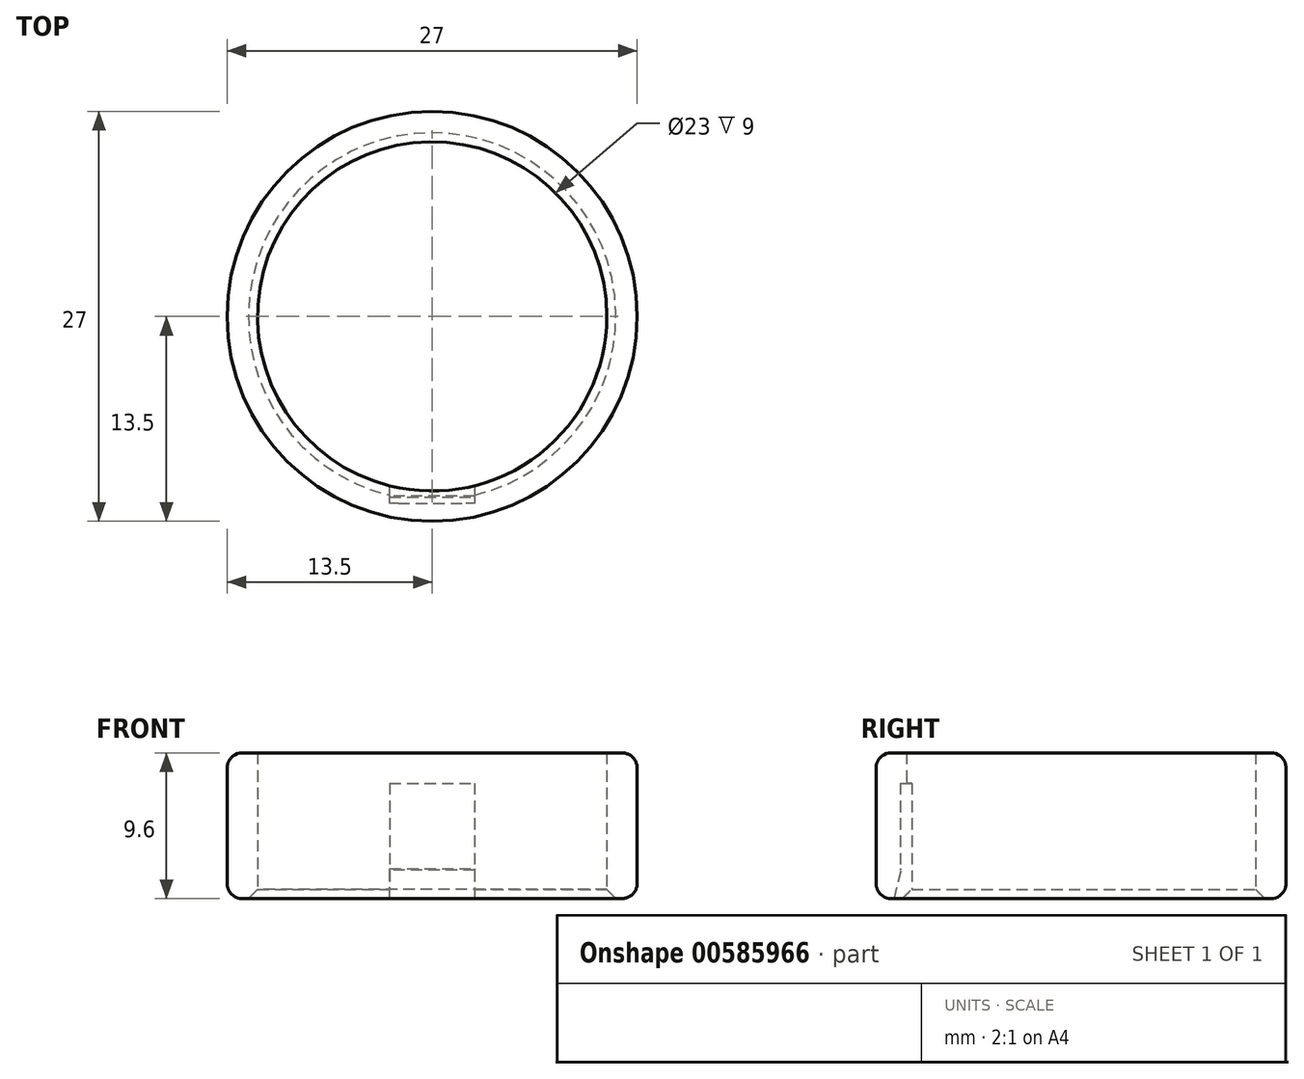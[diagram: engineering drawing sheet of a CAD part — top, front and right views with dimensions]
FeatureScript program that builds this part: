
annotation { "Feature Type Name" : "Feature", "Feature Type Description" : "" }
export const myFeature = defineFeature(function(context is Context, id is Id, definition is map)
    precondition{}
    {
        {
            var Q0;
            Q0=qCreatedBy(makeId("Top.planeOp"),FACE);
            var sketch = newSketch(context, id + "F0", { "sketchPlane" : qUnion([Q0])});
            skCircle(sketch, "E0", {"center": v(0, 0) * mm, "radius": 11.5 * mm});
            skCircle(sketch, "E1", {"center": v(0, 0) * mm, "radius": 13.5 * mm});
            skSolve(sketch);
        }
        {
            var Q0;
            Q0=makeQuery(id+"F0.imprint","IMPRINT",FACE,{"disambiguationData":[TD([[makeQuery(id+"F0.imprint","IMPRINT",EDGE,{"derivedFrom":sQuery(id+"F0.wireOp",EDGE,"E0")}),-1.0]])]});
            extrude(context, id + "F1", {"entities" : qUnion([Q0]), "depth" : 9.6 * mm, "offsetDistance" : 25 * mm});
        }
        {
            var Q0;
            Q0=makeQuery(id+"F0.imprint","IMPRINT",FACE,{"disambiguationData":[TD([[makeQuery(id+"F0.imprint","IMPRINT",EDGE,{"derivedFrom":sQuery(id+"F0.wireOp",EDGE,"E0")}),1.0]])]});
            var sketch = newSketch(context, id + "F2", { "sketchPlane" : qUnion([Q0])});
            skLineSegment(sketch, "E2", {"start": v(0, 0) * mm, "end": v(0, -11.5) * mm, "construction": true});
            skLineSegment(sketch, "E3", {"start": v(0, -11.5) * mm, "end": v(2.8, -11.5) * mm, "construction": true});
            skLineSegment(sketch, "E4", {"start": v(2.8, -11.5) * mm, "end": v(2.8, -12.3) * mm});
            skLineSegment(sketch, "E5", {"start": v(2.8, -12.3) * mm, "end": v(-2.8, -12.3) * mm});
            skLineSegment(sketch, "E6", {"start": v(-2.8, -12.3) * mm, "end": v(-2.8, -11.5) * mm});
            skLineSegment(sketch, "E7", {"start": v(-2.8, -11.5) * mm, "end": v(0, -11.5) * mm, "construction": true});
            skLineSegment(sketch, "E8", {"start": v(-2.8, -11.5) * mm, "end": v(-2.8, -11.1) * mm});
            skLineSegment(sketch, "E9", {"start": v(-2.8, -11.1) * mm, "end": v(2.8, -11.1) * mm});
            skLineSegment(sketch, "E10", {"start": v(2.8, -11.1) * mm, "end": v(2.8, -11.5) * mm});
            skSolve(sketch);
        }
        {
            var Q0;
            Q0 = qSketchRegion(id + "F2", true);
            extrude(context, id + "F3", {"entities" : qUnion([Q0]), "operationType" : NewBodyOperationType.REMOVE, "depth" : 7.6 * mm, "offsetDistance" : 25 * mm});
        }
        {
            var Q0;
            Q0=makeQuery(id+"F3.boolean.opBoolean","COPY",FACE,{"derivedFrom":makeQuery(id+"F3.opExtrude","CAP_FACE",FACE,{"disambiguationData":[OSD([sQuery(id+"F2.wireOp",EDGE,"E4"),sQuery(id+"F2.wireOp",EDGE,"E5"),sQuery(id+"F2.wireOp",EDGE,"E6"),sQuery(id+"F2.wireOp",EDGE,"E8"),sQuery(id+"F2.wireOp",EDGE,"E9"),sQuery(id+"F2.wireOp",EDGE,"E10")])],"isStart":false})});
            cPlane(context, id + "F4", {"entities" : qUnion([Q0]), "cplaneType" : CPlaneType.OFFSET, "offset" : 5.6 * mm, "width" : 150 * mm, "height" : 150 * mm});
        }
        {
            var Q0;
            Q0=qCreatedBy(id+"F4.planeOp",FACE);
            var sketch = newSketch(context, id + "F5", { "sketchPlane" : qUnion([Q0])});
            skLineSegment(sketch, "E11", {"start": v(0, 0) * mm, "end": v(-2.8, 0) * mm, "construction": true});
            skLineSegment(sketch, "E12", {"start": v(-2.8, 0) * mm, "end": v(-2.8, 12.3) * mm, "construction": true});
            skLineSegment(sketch, "E13.bottom", {"start": v(-2.8, 12.3) * mm, "end": v(2.8, 12.3) * mm});
            skLineSegment(sketch, "E13.top", {"start": v(-2.8, 11.9) * mm, "end": v(2.8, 11.9) * mm});
            skLineSegment(sketch, "E13.left", {"start": v(-2.8, 12.3) * mm, "end": v(-2.8, 11.9) * mm});
            skLineSegment(sketch, "E13.right", {"start": v(2.8, 12.3) * mm, "end": v(2.8, 11.9) * mm});
            skSolve(sketch);
        }
        {
            var Q0;
            Q0=makeQuery(id+"F5.imprint","IMPRINT",FACE,{"disambiguationData":[TD([[makeQuery(id+"F5.imprint","IMPRINT",EDGE,{"derivedFrom":sQuery(id+"F5.wireOp",EDGE,"E13.bottom")}),-1.0]])]});
            extrude(context, id + "F6", {"entities" : qUnion([Q0]), "operationType" : NewBodyOperationType.ADD, "oppositeDirection" : true, "depth" : 5.6 * mm, "offsetDistance" : 25 * mm});
        }
        {
            var Q0;
            Q0=makeQuery(id+"F5.imprint","IMPRINT",FACE,{"disambiguationData":[TD([[makeQuery(id+"F5.imprint","IMPRINT",EDGE,{"derivedFrom":sQuery(id+"F5.wireOp",EDGE,"E13.bottom")}),-1.0]])]});
            var sketch = newSketch(context, id + "F7", { "sketchPlane" : qUnion([Q0])});
            skLineSegment(sketch, "E14", {"start": v(0, 0) * mm, "end": v(-2.8, 0) * mm, "construction": true});
            skLineSegment(sketch, "E15", {"start": v(-2.8, 0) * mm, "end": v(-2.8, 11.8) * mm, "construction": true});
            skLineSegment(sketch, "E16.bottom", {"start": v(-2.8, 11.8) * mm, "end": v(2.8, 11.8) * mm});
            skLineSegment(sketch, "E16.top", {"start": v(-2.8, 12.3) * mm, "end": v(2.8, 12.3) * mm});
            skLineSegment(sketch, "E16.left", {"start": v(-2.8, 11.8) * mm, "end": v(-2.8, 12.3) * mm});
            skLineSegment(sketch, "E16.right", {"start": v(2.8, 11.8) * mm, "end": v(2.8, 12.3) * mm});
            skSolve(sketch);
        }
        {
            var Q0;
            Q0 = qSketchRegion(id + "F7", true);
            extrude(context, id + "F8", {"entities" : qUnion([Q0]), "operationType" : NewBodyOperationType.ADD, "depth" : 2 * mm, "offsetDistance" : 25 * mm});
        }
        {
            var Q0;
            Q0=makeQuery(id+"F8.opExtrude","CAP_EDGE",EDGE,{"disambiguationData":[OSD([sQuery(id+"F7.wireOp",EDGE,"E16.bottom")])],"isStart":false});
            chamfer(context, id + "F9", {"entities" : qUnion([Q0]), "chamferType" : ChamferType.TWO_OFFSETS, "width1" : 0.5 * mm, "oppositeDirection" : false, "width2" : 2 * mm, "tangentPropagation" : true});
        }
        {
            var Q0;
            {var subQ0=sQuery(id+"F7.wireOp",EDGE,"E16.bottom");Q0=makeQuery(id+"F9.opChamfer","BLEND_EDGE",EDGE,{"blendedFrom":[makeQuery(id+"F8.opExtrude","CAP_EDGE",EDGE,{"disambiguationData":[OSD([subQ0])],"isStart":false}),makeQuery(id+"F8.opExtrude","CAP_FACE",FACE,{"disambiguationData":[OSD([subQ0,sQuery(id+"F7.wireOp",EDGE,"E16.top"),sQuery(id+"F7.wireOp",EDGE,"E16.left"),sQuery(id+"F7.wireOp",EDGE,"E16.right")])],"isStart":true})],"blendedInto":[makeQuery(id+"F8.opExtrude","CAP_FACE",FACE,{"disambiguationData":[OSD([subQ0,sQuery(id+"F7.wireOp",EDGE,"E16.top"),sQuery(id+"F7.wireOp",EDGE,"E16.left"),sQuery(id+"F7.wireOp",EDGE,"E16.right")])],"isStart":true})]});}
            chamfer(context, id + "F10", {"entities" : qUnion([Q0]), "width" : .1 * mm, "tangentPropagation" : true});
        }
        {
            var Q0;
            Q0=makeQuery(id+"F1.opExtrude","CAP_EDGE",EDGE,{"disambiguationData":[OSD([sQuery(id+"F0.wireOp",EDGE,"E1")])],"isStart":false});
            var Q1;
            Q1=makeQuery(id+"F1.opExtrude","CAP_EDGE",EDGE,{"disambiguationData":[OSD([sQuery(id+"F0.wireOp",EDGE,"E1")])],"isStart":true});
            fillet(context, id + "F11", {"entities" : qUnion([Q0, Q1]), "radius" : 1 * mm, "tangentPropagation" : true, "allowEdgeOverflow" : false});
        }
        {
            var Q0;
            Q0=makeQuery(id+"F1.opExtrude","CAP_EDGE",EDGE,{"disambiguationData":[OSD([sQuery(id+"F0.wireOp",EDGE,"E0")])],"isStart":true});
            chamfer(context, id + "F12", {"entities" : qUnion([Q0]), "width" : .6 * mm, "tangentPropagation" : true});
        }
    });
